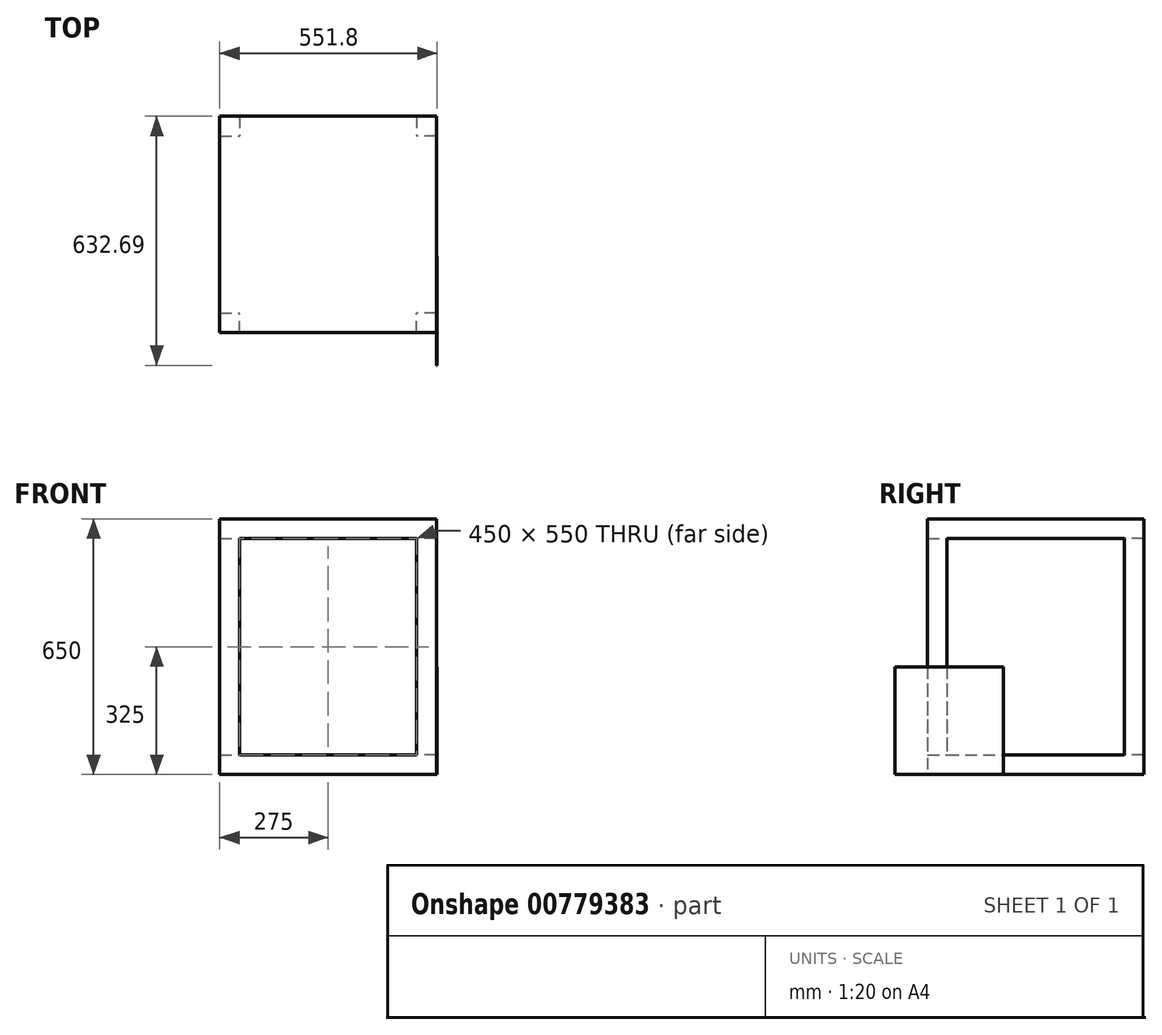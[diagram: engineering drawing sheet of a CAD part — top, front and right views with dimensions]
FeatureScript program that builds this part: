
annotation { "Feature Type Name" : "Feature", "Feature Type Description" : "" }
export const myFeature = defineFeature(function(context is Context, id is Id, definition is map)
    precondition{}
    {
        {
            var Q0;
            Q0=qCreatedBy(makeId("Top.planeOp"),FACE);
            var sketch = newSketch(context, id + "F0", { "sketchPlane" : qUnion([Q0])});
            skLineSegment(sketch, "E0.bottom", {"start": v(0, 0) * mm, "end": v(-550, 0) * mm});
            skLineSegment(sketch, "E0.top", {"start": v(0, 550) * mm, "end": v(-550, 550) * mm});
            skLineSegment(sketch, "E0.left", {"start": v(0, 0) * mm, "end": v(0, 550) * mm});
            skLineSegment(sketch, "E0.right", {"start": v(-550, 0) * mm, "end": v(-550, 550) * mm});
            skSolve(sketch);
        }
        {
            var Q0;
            Q0=makeQuery(id+"F0.imprint","IMPRINT",FACE,{"disambiguationData":[TD([[makeQuery(id+"F0.imprint","IMPRINT",EDGE,{"derivedFrom":sQuery(id+"F0.wireOp",EDGE,"E0.bottom")}),-1.0]])]});
            extrude(context, id + "F1", {"entities" : qUnion([Q0]), "depth" : 50 * mm, "offsetDistance" : 25 * mm});
        }
        {
            var Q0;
            Q0=makeQuery(id+"F1.opExtrude","CAP_FACE",FACE,{"disambiguationData":[OSD([sQuery(id+"F0.wireOp",EDGE,"E0.bottom"),sQuery(id+"F0.wireOp",EDGE,"E0.top"),sQuery(id+"F0.wireOp",EDGE,"E0.left"),sQuery(id+"F0.wireOp",EDGE,"E0.right")])],"isStart":false});
            var sketch = newSketch(context, id + "F2", { "sketchPlane" : qUnion([Q0])});
            skLineSegment(sketch, "E1.bottom", {"start": v(-550, 0) * mm, "end": v(-500, 0) * mm});
            skLineSegment(sketch, "E1.top", {"start": v(-550, 50) * mm, "end": v(-500, 50) * mm});
            skLineSegment(sketch, "E1.left", {"start": v(-550, 0) * mm, "end": v(-550, 50) * mm});
            skLineSegment(sketch, "E1.right", {"start": v(-500, 0) * mm, "end": v(-500, 50) * mm});
            skLineSegment(sketch, "E2.bottom", {"start": v(0, 0) * mm, "end": v(-50, 0) * mm});
            skLineSegment(sketch, "E2.top", {"start": v(0, 50) * mm, "end": v(-50, 50) * mm});
            skLineSegment(sketch, "E2.left", {"start": v(0, 0) * mm, "end": v(0, 50) * mm});
            skLineSegment(sketch, "E2.right", {"start": v(-50, 0) * mm, "end": v(-50, 50) * mm});
            skLineSegment(sketch, "E3.bottom", {"start": v(0, 550) * mm, "end": v(-50, 550) * mm});
            skLineSegment(sketch, "E3.top", {"start": v(0, 500) * mm, "end": v(-50, 500) * mm});
            skLineSegment(sketch, "E3.left", {"start": v(0, 550) * mm, "end": v(0, 500) * mm});
            skLineSegment(sketch, "E3.right", {"start": v(-50, 550) * mm, "end": v(-50, 500) * mm});
            skLineSegment(sketch, "E4.bottom", {"start": v(-550, 550) * mm, "end": v(-500, 550) * mm});
            skLineSegment(sketch, "E4.top", {"start": v(-550, 500) * mm, "end": v(-500, 500) * mm});
            skLineSegment(sketch, "E4.left", {"start": v(-550, 550) * mm, "end": v(-550, 500) * mm});
            skLineSegment(sketch, "E4.right", {"start": v(-500, 550) * mm, "end": v(-500, 500) * mm});
            skSolve(sketch);
        }
        {
            var Q0;
            Q0=makeQuery(id+"F2.imprint","IMPRINT",FACE,{"disambiguationData":[TD([[makeQuery(id+"F2.imprint","IMPRINT",EDGE,{"derivedFrom":sQuery(id+"F2.wireOp",EDGE,"E4.bottom")}),1.0]])]});
            var Q1;
            Q1=makeQuery(id+"F2.imprint","IMPRINT",FACE,{"disambiguationData":[TD([[makeQuery(id+"F2.imprint","IMPRINT",EDGE,{"derivedFrom":sQuery(id+"F2.wireOp",EDGE,"E1.bottom")}),-1.0]])]});
            var Q2;
            Q2=makeQuery(id+"F2.imprint","IMPRINT",FACE,{"disambiguationData":[TD([[makeQuery(id+"F2.imprint","IMPRINT",EDGE,{"derivedFrom":sQuery(id+"F2.wireOp",EDGE,"E2.bottom")}),-1.0]])]});
            var Q3;
            Q3=makeQuery(id+"F2.imprint","IMPRINT",FACE,{"disambiguationData":[TD([[makeQuery(id+"F2.imprint","IMPRINT",EDGE,{"derivedFrom":sQuery(id+"F2.wireOp",EDGE,"E3.bottom")}),1.0]])]});
            extrude(context, id + "F3", {"entities" : qUnion([Q0, Q1, Q2, Q3]), "operationType" : NewBodyOperationType.ADD, "depth" : 550 * mm, "offsetDistance" : 25 * mm});
        }
        {
            var Q0;
            Q0=makeQuery(id+"F3.opExtrude","CAP_FACE",FACE,{"disambiguationData":[OSD([sQuery(id+"F2.wireOp",EDGE,"E4.bottom"),sQuery(id+"F2.wireOp",EDGE,"E4.top"),sQuery(id+"F2.wireOp",EDGE,"E4.left"),sQuery(id+"F2.wireOp",EDGE,"E4.right")])],"isStart":false});
            var sketch = newSketch(context, id + "F4", { "sketchPlane" : qUnion([Q0])});
            skLineSegment(sketch, "E5.bottom", {"start": v(-550, 550) * mm, "end": v(0, 550) * mm});
            skLineSegment(sketch, "E5.top", {"start": v(-550, 0) * mm, "end": v(0, 0) * mm});
            skLineSegment(sketch, "E5.left", {"start": v(-550, 550) * mm, "end": v(-550, 0) * mm});
            skLineSegment(sketch, "E5.right", {"start": v(0, 550) * mm, "end": v(0, 0) * mm});
            skSolve(sketch);
        }
        {
            var Q0;
            {var subQ4=makeQuery(id+"F3.opExtrude","CAP_EDGE",EDGE,{"disambiguationData":[OSD([sQuery(id+"F2.wireOp",EDGE,"E4.top")])],"isStart":false});Q0=makeQuery(id+"F4.imprint","IMPRINT",FACE,{"disambiguationData":[TD([[makeQuery(id+"F4.imprint","IMPRINT",EDGE,{"derivedFrom":subQ4}),1.0]])]});}
            var Q1;
            {var subQ2=sQuery(id+"F4.wireOp",EDGE,"E5.top");Q1=makeQuery(id+"F4.imprint","IMPRINT",FACE,{"disambiguationData":[TD([[makeQuery(id+"F4.imprint","IMPRINT",EDGE,{"derivedFrom":subQ2}),1.0]])]});}
            extrude(context, id + "F5", {"entities" : qUnion([Q0, Q1]), "operationType" : NewBodyOperationType.ADD, "depth" : 50 * mm, "offsetDistance" : 25 * mm});
        }
        {
            var Q0;
            Q0=makeQuery(id+"F5.boolean.opBoolean","MERGE",FACE,{"derivedFrom":[makeQuery(id+"F3.boolean.opBoolean","MERGE",FACE,{"derivedFrom":[makeQuery(id+"F1.opExtrude","SWEPT_FACE",FACE,{"disambiguationData":[OSD([sQuery(id+"F0.wireOp",EDGE,"E0.left")])]}),makeQuery(id+"F3.opExtrude","SWEPT_FACE",FACE,{"disambiguationData":[OSD([sQuery(id+"F2.wireOp",EDGE,"E2.left")])]}),makeQuery(id+"F3.opExtrude","SWEPT_FACE",FACE,{"disambiguationData":[OSD([sQuery(id+"F2.wireOp",EDGE,"E3.left")])]})]}),makeQuery(id+"F5.opExtrude","SWEPT_FACE",FACE,{"disambiguationData":[OSD([sQuery(id+"F4.wireOp",EDGE,"E5.right")])]})]});
            var sketch = newSketch(context, id + "F6", { "sketchPlane" : qUnion([Q0])});
            skLineSegment(sketch, "E6.bottom", {"start": v(193.7, 0) * mm, "end": v(-82.7, 0) * mm});
            skLineSegment(sketch, "E6.top", {"start": v(193.7, 273.04) * mm, "end": v(-82.7, 273.04) * mm});
            skLineSegment(sketch, "E6.left", {"start": v(193.7, 0) * mm, "end": v(193.7, 273.04) * mm});
            skLineSegment(sketch, "E6.right", {"start": v(-82.7, 0) * mm, "end": v(-82.7, 273.04) * mm});
            skSolve(sketch);
        }
        {
            var Q0;
            {var subQ3=sQuery(id+"F6.wireOp",EDGE,"E6.right");Q0=makeQuery(id+"F6.imprint","IMPRINT",FACE,{"disambiguationData":[TD([[makeQuery(id+"F6.imprint","IMPRINT",EDGE,{"derivedFrom":subQ3}),-1.0]])]});}
            var Q1;
            {var subQ0=sQuery(id+"F0.wireOp",EDGE,"E0.left");var subQ1=makeQuery(id+"F1.opExtrude","CAP_EDGE",EDGE,{"disambiguationData":[OSD([subQ0])],"isStart":false});var subQ9=sQuery(id+"F6.wireOp",EDGE,"E6.left");var subQ12=makeQuery(id+"F6.imprint","INTERSECT",VERTEX,{"derivedFrom":[subQ1,subQ9]});Q1=makeQuery(id+"F6.imprint","IMPRINT",FACE,{"disambiguationData":[TD([[makeQuery(id+"F6.imprint","IMPRINT",EDGE,{"disambiguationData":[TD([[subQ12,1.0]])],"derivedFrom":subQ9}),1.0]])]});}
            var Q2;
            {var subQ0=sQuery(id+"F6.wireOp",EDGE,"E6.left");var subQ1=sQuery(id+"F6.wireOp",EDGE,"E6.top");var subQ2=makeQuery(id+"F6.imprint","INTERSECT",VERTEX,{"derivedFrom":[subQ1,subQ0]});Q2=makeQuery(id+"F6.imprint","IMPRINT",FACE,{"disambiguationData":[TD([[makeQuery(id+"F6.imprint","IMPRINT",EDGE,{"disambiguationData":[TD([[subQ2,1.0]])],"derivedFrom":subQ0}),1.0]])]});}
            extrude(context, id + "F7", {"entities" : qUnion([Q0, Q1, Q2]), "operationType" : NewBodyOperationType.ADD, "depth" : 1.8 * mm, "offsetDistance" : 25 * mm});
        }
    });
